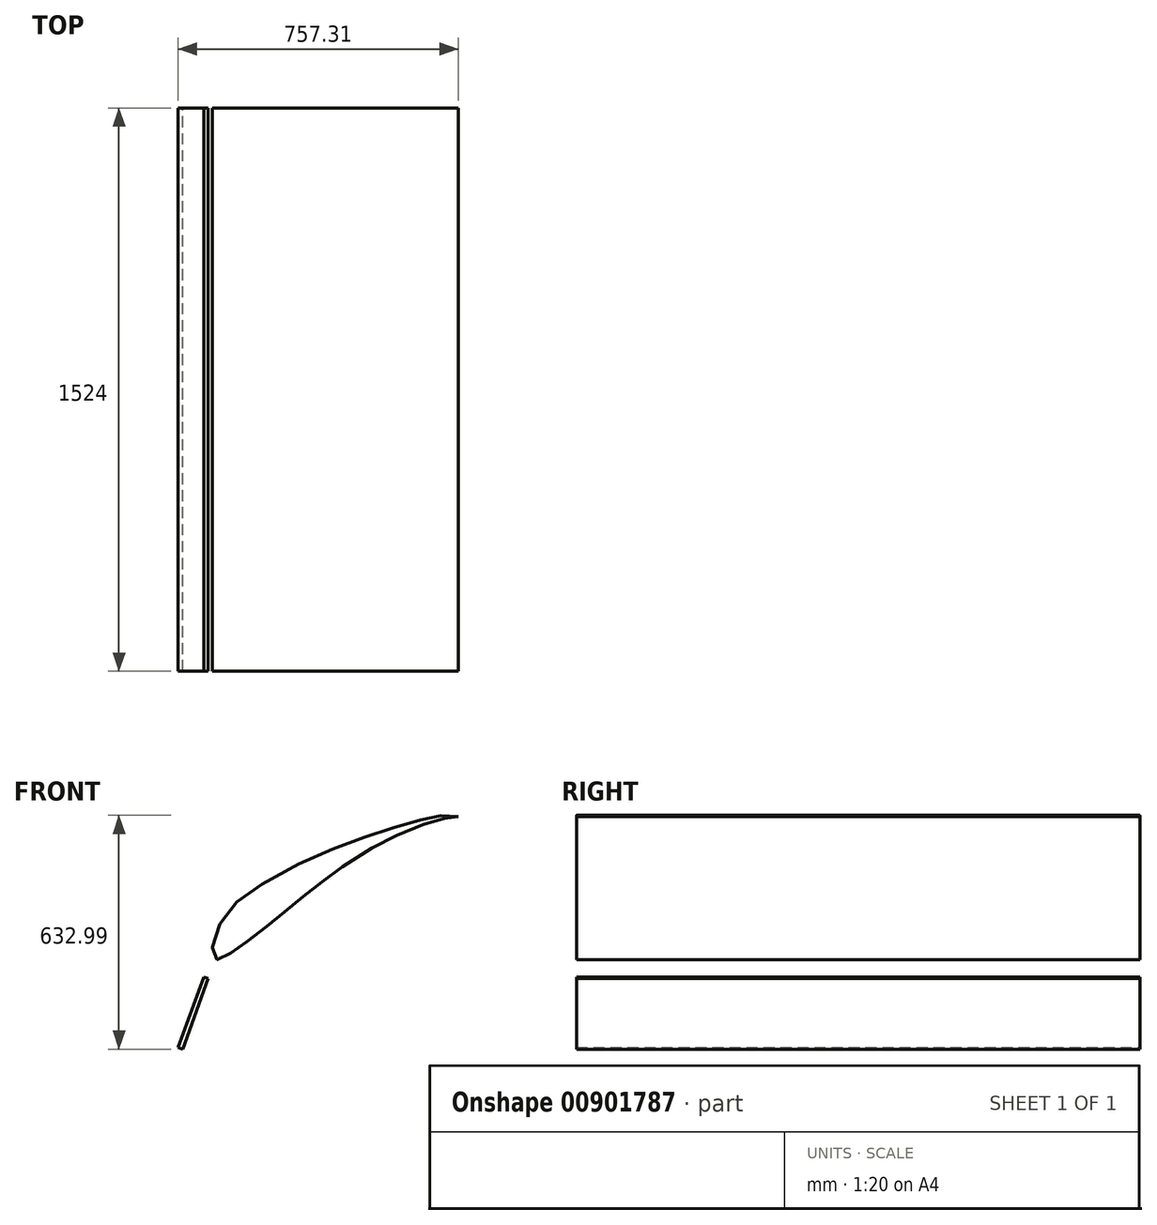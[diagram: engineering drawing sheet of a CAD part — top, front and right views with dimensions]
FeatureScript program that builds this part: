
annotation { "Feature Type Name" : "Feature", "Feature Type Description" : "" }
export const myFeature = defineFeature(function(context is Context, id is Id, definition is map)
    precondition{}
    {
        {
            var Q0;
            Q0=qCreatedBy(makeId("Front.planeOp"),FACE);
            var sketch = newSketch(context, id + "F0", { "sketchPlane" : qUnion([Q0])});
            skLineSegment(sketch, "E0", {"start": v(22.7, 50.08) * mm, "end": v(784.7, 50.08) * mm});
            skFitSpline(sketch, "E1", {"points": [v(745.37, 629.1) * mm, v(740.46, 628.9) * mm, v(731.32, 628.58) * mm, v(720.73, 627.42) * mm, v(709.06, 625.28) * mm, v(690.16, 620.81) * mm, v(669.26, 614.53) * mm, v(644.34, 605.92) * mm, v(611.01, 592.81) * mm, v(568.77, 574.28) * mm, v(530.47, 554.77) * mm, v(508.15, 542.52) * mm, v(450.9, 506.86) * mm, v(418.72, 484.47) * mm, v(394.9, 466.98) * mm, v(372.25, 449.81) * mm, v(351.24, 433.32) * mm, v(330.58, 417.09) * mm, v(309.18, 399.58) * mm, v(287.1, 381.4) * mm, v(266.43, 364.47) * mm, v(245.7, 347.14) * mm, v(227.09, 331.74) * mm, v(203.48, 312.69) * mm, v(181.2, 295.73) * mm, v(162.05, 281.5) * mm, v(161.05, 280.79) * mm, v(146.62, 270.98) * mm, v(125.42, 257.4) * mm, v(111.71, 249.27) * mm, v(103.45, 245.14) * mm, v(97.11, 242.82) * mm, v(91.73, 242.74) * mm, v(87.25, 244.53) * mm, v(84.5, 247.55) * mm, v(81.38, 256.86) * mm, v(80.38, 274.58) * mm, v(84.66, 299.66) * mm, v(94.98, 327.6) * mm, v(112.36, 359) * mm, v(133.2, 385.5) * mm, v(164.2, 413.54) * mm, v(198.87, 437.4) * mm, v(268.62, 477.73) * mm, v(337.31, 511.6) * mm, v(395.5, 536.87) * mm, v(450.36, 558.34) * mm, v(497.09, 574.67) * mm, v(535, 588.1) * mm, v(579.25, 602.27) * mm, v(613.36, 612.43) * mm, v(651.42, 622.41) * mm, v(670.38, 626.6) * mm, v(689.25, 630.11) * mm, v(707.84, 632.54) * mm, v(727.58, 632.71) * mm, v(737.64, 630.99) * mm, v(745.37, 629.1) * mm]});
            skLineSegment(sketch, "E2.bottom", {"start": v(0, 0) * mm, "end": v(69.5, 190.95) * mm});
            skLineSegment(sketch, "E2.top", {"start": v(-11.93, 4.34) * mm, "end": v(57.56, 195.29) * mm});
            skLineSegment(sketch, "E2.left", {"start": v(0, 0) * mm, "end": v(-11.93, 4.34) * mm});
            skLineSegment(sketch, "E2.right", {"start": v(69.5, 190.95) * mm, "end": v(57.56, 195.29) * mm});
            skSolve(sketch);
        }
        {
            var Q0;
            Q0=makeQuery(id+"F0.imprint","IMPRINT",FACE,{"disambiguationData":[TD([[makeQuery(id+"F0.imprint","IMPRINT",EDGE,{"derivedFrom":sQuery(id+"F0.wireOp",EDGE,"E1")}),-1.0]])]});
            extrude(context, id + "F1", {"entities" : qUnion([Q0]), "depth" : 1524 * mm, "offsetDistance" : 25 * mm});
        }
        {
            var Q0;
            Q0=makeQuery(id+"F0.imprint","IMPRINT",FACE,{"disambiguationData":[TD([[makeQuery(id+"F0.imprint","IMPRINT",EDGE,{"derivedFrom":sQuery(id+"F0.wireOp",EDGE,"E2.bottom")}),1.0]])]});
            extrude(context, id + "F2", {"entities" : qUnion([Q0]), "depth" : 1524 * mm, "offsetDistance" : 25 * mm});
        }
    });
